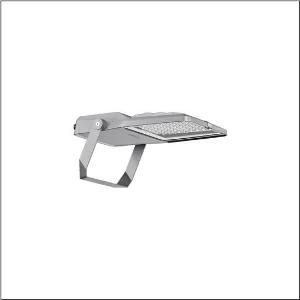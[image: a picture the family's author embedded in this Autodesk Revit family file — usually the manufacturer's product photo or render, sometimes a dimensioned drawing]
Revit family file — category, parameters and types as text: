
# Revit family: floodlight_fl_21_iq_mini___pl33t_5xa7772c4f1a_48c1
name_source: partatom
category: Lighting Fixtures
units: mm (PartAtom-declared; Revit-internal decimal feet)

## family parameters
Cut with Voids When Loaded = No
Host = Face
Light Source = No
Part Type = Normal
Room Calculation Point = No
Round Connector Dimension = Use Diameter
Shared = No

## types (1)
- --- (1 x LED, 12570 lm, 87.2 W, 4000K)
    Apparent Load = 87 VA
    CIE Flux Codes = 26 75 99 100 100
    Color Rendering = 70
    Color Temperature = 4000K
    Default Elevation = 1800 mm
    Description = Floodlight FL 21 iQ mini, floodlight, primary light control with lens, of PMMA, primary optical cover: protective disc, of toughened safety glass, transparent, light distribution: PL33T, light emission: direct distribution, installation type: surface-mounted, LED, High Power LED, rated luminous flux: 12.570lm, luminous efficacy: 144lm/W, light colour: 740, colour temperature: 4000K, control: Street-Remote, Auto-Match, Temp-Guard, Night-Set, Smart-Wire, Desk-Remote (wireless, voltage-free reading and setting of iQ features in the workshop via application-optimized NFC function/RFID function), optimised constant luminous flux control (CLO 2.0), with terminal, 6-pole, mains connection: 220..240V, AC, 50/60Hz, start of lifetime: 87W, end of service life: 92W, reduction: 40W, luminaire housing, of diecast aluminium, powder-coated, Siteco® metallic grey (DB 702S), corrosivity category C5 mid according to DIN EN ISO 12944, sealing non-destructively replaceable, mounting bracket, of steel, galvanised, powder-coated, Siteco® metallic grey (DB 702S), protection rating (complete): IP66, insulation class (complete): insulation class II (safety insulation), certification: CE, ENEC, VDE, protection symbol: D, impact resistance: IK08, permissible operating ambient temperature: -40..+40°C, permissible operating ambient temperature for outdoor applications: -40..+50°C, standard: DIN EN 12944, LABS conformity tested according to VDMA 24364:2018-05, packaging unit: 1 piece

Light Distribution: PL33T
    Height = 70 mm
    Lamp = 1 x LED
    Lamp Light Flux = 12570 lm
    Lamp Power = 87.2 W
    Lamp count = 1
    Length = 485 mm
    Luminous efficacy = 144 lm/W
    Manufacturer = Siteco
    ModVariant = No
    Model = 5XA7772C4F1A
    Number of Poles = 1
    OnlyDefault = Yes
    Power Factor = 1
    Product Name = Floodlight FL 21 iQ mini | PL33T
    Product group = floodlight | pylon annexe
    ProductGroupID = 6200
    Protection Class = Protection class II
    Protection Degree = IP 66
    RLX_Detail_Level = 1
    RLX_Emergency_Light_Flux = 0 lm
    RLX_Emergency_Type = 0
    RLX_Emergency_Type_DB = No
    RlxData = <blob elided: 96281 chars, md5=a4a2af13>
    Socket = socket
    Standby Power = 0 W
    System Light Flux = 12570 lm
    System Power = 87 W
    Type Comments = factory setting: luminous flux: 100 % | dim-lin: 254 | 456 mA
    Type Image = l_1006845.jpg
    URL = http://relux.com
    VarID = @adj_081903
    Voltage = 0 V
    Weight = 0.00 kg
    Width = 337 mm

## geometry (parser evidence)
native form markers: Blend x4, Sweep x10
no freeform markers — native parametric forms only
